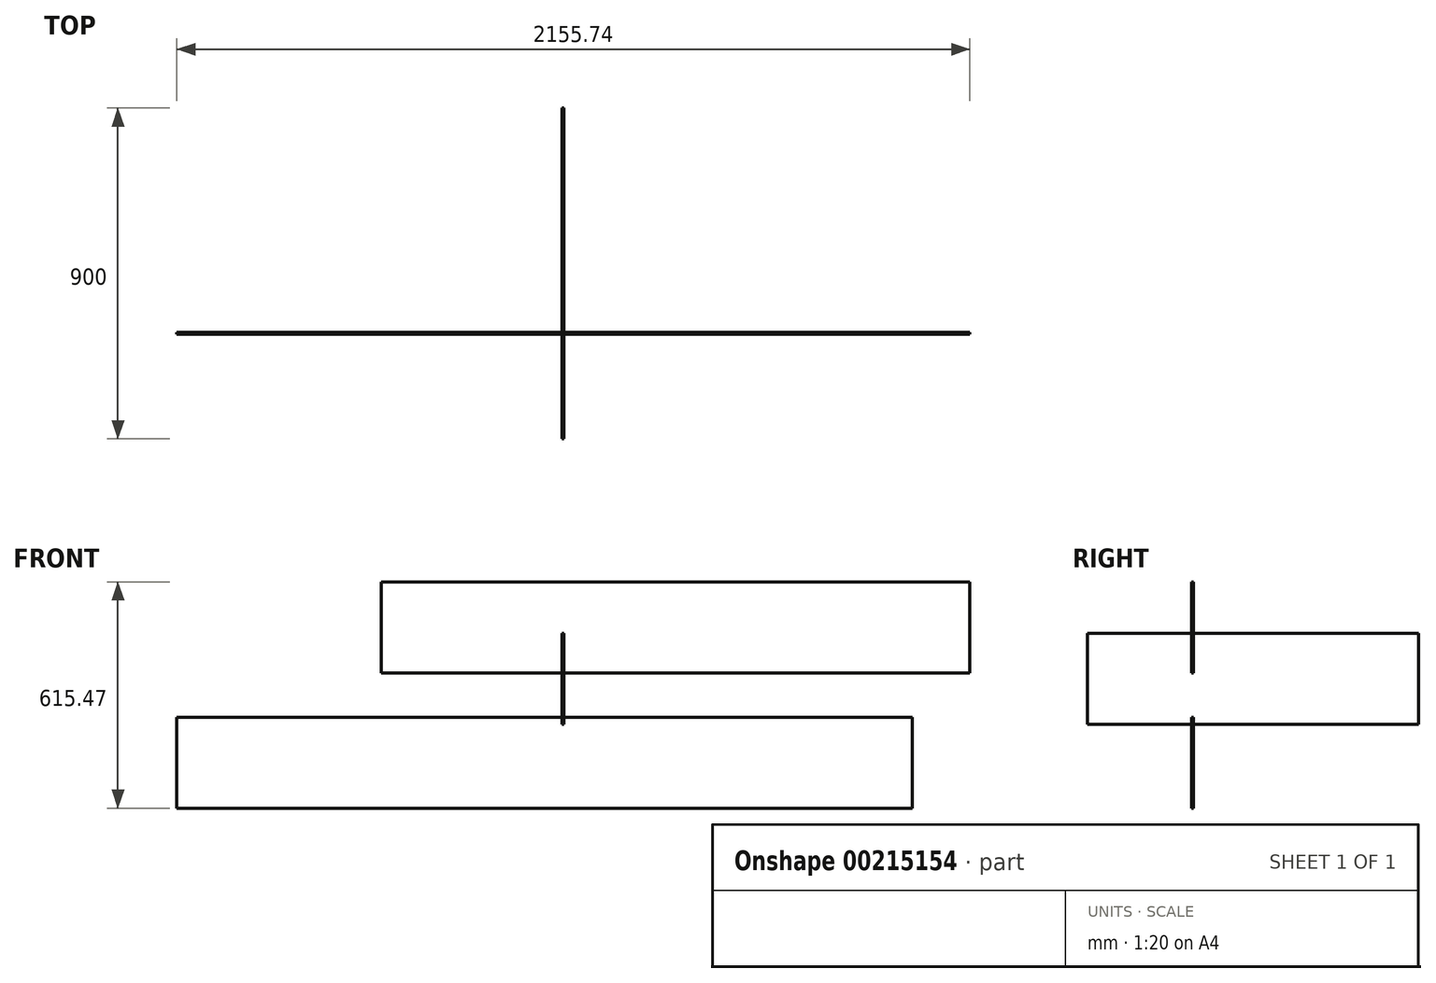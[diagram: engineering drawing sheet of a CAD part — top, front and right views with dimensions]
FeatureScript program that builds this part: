
annotation { "Feature Type Name" : "Feature", "Feature Type Description" : "" }
export const myFeature = defineFeature(function(context is Context, id is Id, definition is map)
    precondition{}
    {
        {
            var Q0;
            Q0=qCreatedBy(makeId("Front.planeOp"),FACE);
            var sketch = newSketch(context, id + "F0", { "sketchPlane" : qUnion([Q0])});
            skLineSegment(sketch, "E0.bottom", {"start": v(-1047.52, -121.47) * mm, "end": v(952.48, -121.47) * mm});
            skLineSegment(sketch, "E0.top", {"start": v(-1047.52, -368.47) * mm, "end": v(952.48, -368.47) * mm});
            skLineSegment(sketch, "E0.left", {"start": v(-1047.52, -121.47) * mm, "end": v(-1047.52, -368.47) * mm});
            skLineSegment(sketch, "E0.right", {"start": v(952.48, -121.47) * mm, "end": v(952.48, -368.47) * mm});
            skSolve(sketch);
        }
        {
            var Q0;
            Q0 = qSketchRegion(id + "F0", true);
            extrude(context, id + "F1", {"entities" : qUnion([Q0]), "depth" : 5 * mm});
        }
        {
            var Q0;
            Q0=qCreatedBy(makeId("Right.planeOp"),FACE);
            var sketch = newSketch(context, id + "F2", { "sketchPlane" : qUnion([Q0])});
            skLineSegment(sketch, "E1.bottom", {"start": v(611.02, 107) * mm, "end": v(-288.98, 107) * mm});
            skLineSegment(sketch, "E1.top", {"start": v(611.02, -140) * mm, "end": v(-288.98, -140) * mm});
            skLineSegment(sketch, "E1.left", {"start": v(611.02, 107) * mm, "end": v(611.02, -140) * mm});
            skLineSegment(sketch, "E1.right", {"start": v(-288.98, 107) * mm, "end": v(-288.98, -140) * mm});
            skSolve(sketch);
        }
        {
            var Q0;
            Q0=qCreatedBy(makeId("Front.planeOp"),FACE);
            var sketch = newSketch(context, id + "F3", { "sketchPlane" : qUnion([Q0])});
            skLineSegment(sketch, "E2.bottom", {"start": v(-491.78, 247) * mm, "end": v(1108.22, 247) * mm});
            skLineSegment(sketch, "E2.top", {"start": v(-491.78, 0) * mm, "end": v(1108.22, 0) * mm});
            skLineSegment(sketch, "E2.left", {"start": v(-491.78, 247) * mm, "end": v(-491.78, 0) * mm});
            skLineSegment(sketch, "E2.right", {"start": v(1108.22, 247) * mm, "end": v(1108.22, 0) * mm});
            skSolve(sketch);
        }
        {
            var Q0;
            Q0 = qSketchRegion(id + "F2", true);
            extrude(context, id + "F4", {"entities" : qUnion([Q0]), "depth" : 5 * mm});
        }
        {
            var Q0;
            Q0 = qSketchRegion(id + "F3", true);
            extrude(context, id + "F5", {"entities" : qUnion([Q0]), "depth" : 5 * mm});
        }
    });
